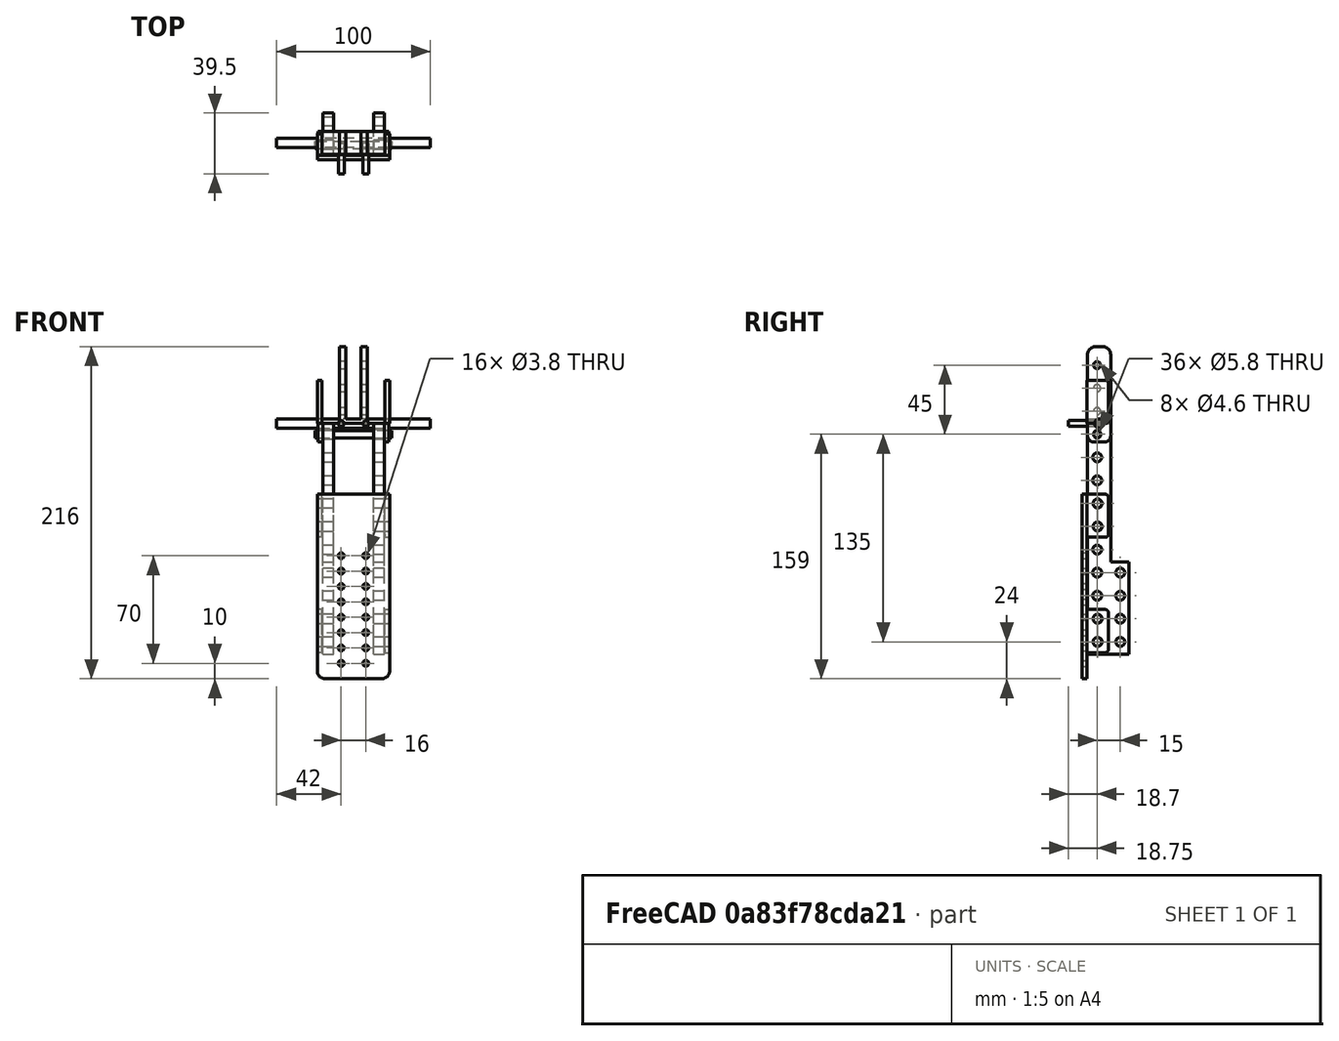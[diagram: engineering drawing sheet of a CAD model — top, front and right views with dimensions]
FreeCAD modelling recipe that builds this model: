
FCSTD DOCUMENT  (FreeCAD 0.20R29410 (Git))
Label: big_cnc_laser_wire_holder
License: All rights reserved
LicenseURL: http://en.wikipedia.org/wiki/All_rights_reserved
objects: Part::Cylinder×83, Part::Box×9, Part::MultiFuse×7, Part::Cut×5, Part::Fuse×4, Part::Fillet×4, Part::Mirroring×4, Part::FeaturePython×4, Part::Compound×2
note: 118 computed .brp shape members not serialized (recipe doc carries the construction recipe); baked Part::Feature solids carry a one-line shape summary decoded from their .brp

FEATURE [Part::Box] cube
  AttacherType = Attacher::AttachEngine3D
  Height = 60
  Length = 7
  Placement = pos=(-3.5,-6,-30) rot=(0,0,1;0rad)
  Width = 12
FEATURE [Part::Box] cube001
  AttacherType = Attacher::AttachEngine3D
  Height = 150
  Length = 7
  Placement = pos=(-3.5,-21,-30) rot=(0,0,1;0rad)
  Width = 15
FEATURE [Part::Fuse] Matrix_Union
  Base = -> cube
  Placement = pos=(16.5,-20,0) rot=(0,0,1;0rad)
  Tool = -> cube001
FEATURE [Part::Cylinder] cylinder
  Angle = 360
  AttacherType = Attacher::AttachEngine3D
  FirstAngle = 0
  Height = 132
  Placement = pos=(-66,0,10) rot=(0,1,0;1.5708rad)
  Radius = 2.9
  SecondAngle = 0
FEATURE [Part::Cylinder] cylinder001 .. cylinder019  x19 (patterned run collapsed; names and placements below)
  Angle = 360
  AttacherType = Attacher::AttachEngine3D
  FirstAngle = 0
  Height = 132
  Radius = 2.9
  SecondAngle = 0
  placements: 19 in arithmetic series — first pos=(-66,0,25) rot=(0,1,0;1.5708rad), step (0,0,15), last pos=(-66,0,295) rot=(0,1,0;1.5708rad)
FEATURE [Part::MultiFuse] Group
  Placement = pos=(0,-19.75,-32) rot=(0,0,1;0rad)
  Shapes = -> [cylinder,cylinder001,cylinder002,cylinder003,cylinder004,cylinder005,cylinder006,cylinder007,cylinder008,cylinder009,cylinder010,cylinder011,cylinder012,cylinder013,cylinder014,cylinder015,cylinder016,cylinder017,cylinder018,cylinder019]
FEATURE [Part::Cylinder] cylinder020 .. cylinder039  x20 (patterned run collapsed; names and placements below)
  Angle = 360
  AttacherType = Attacher::AttachEngine3D
  FirstAngle = 0
  Height = 132
  Radius = 2.9
  SecondAngle = 0
  placements: 20 in arithmetic series — first pos=(-66,0,10) rot=(0,1,0;1.5708rad), step (0,0,15), last pos=(-66,0,295) rot=(0,1,0;1.5708rad)
FEATURE [Part::MultiFuse] Group001
  Placement = pos=(0,-34.75,-32) rot=(0,0,1;0rad)
  Shapes = -> [cylinder020,cylinder021,cylinder022,cylinder023,cylinder024,cylinder025,cylinder026,cylinder027,cylinder028,cylinder029,cylinder030,cylinder031,cylinder032,cylinder033,cylinder034,cylinder035,cylinder036,cylinder037,cylinder038,cylinder039]
FEATURE [Part::Fuse] union
  Base = -> Group
  Tool = -> Group001
FEATURE [Part::Cut] difference
  Base = -> Matrix_Union
  Tool = -> union
FEATURE [Part::Box] cube002
  AttacherType = Attacher::AttachEngine3D
  Height = 60
  Length = 7
  Placement = pos=(-3.5,-6,-30) rot=(0,0,1;0rad)
  Width = 12
FEATURE [Part::Box] cube003
  AttacherType = Attacher::AttachEngine3D
  Height = 150
  Length = 7
  Placement = pos=(-3.5,-21,-30) rot=(0,0,1;0rad)
  Width = 15
FEATURE [Part::Fuse] Matrix_Union001
  Base = -> cube002
  Placement = pos=(-16.5,-20,0) rot=(0,0,1;0rad)
  Tool = -> cube003
FEATURE [Part::Cylinder] cylinder040 .. cylinder059  x20 (patterned run collapsed; names and placements below)
  Angle = 360
  AttacherType = Attacher::AttachEngine3D
  FirstAngle = 0
  Height = 132
  Radius = 2.9
  SecondAngle = 0
  placements: 20 in arithmetic series — first pos=(-66,0,10) rot=(0,1,0;1.5708rad), step (0,0,15), last pos=(-66,0,295) rot=(0,1,0;1.5708rad)
FEATURE [Part::MultiFuse] Group002
  Placement = pos=(0,-19.75,-32) rot=(0,0,1;0rad)
  Shapes = -> [cylinder040,cylinder041,cylinder042,cylinder043,cylinder044,cylinder045,cylinder046,cylinder047,cylinder048,cylinder049,cylinder050,cylinder051,cylinder052,cylinder053,cylinder054,cylinder055,cylinder056,cylinder057,cylinder058,cylinder059]
FEATURE [Part::Cylinder] cylinder060 .. cylinder079  x20 (patterned run collapsed; names and placements below)
  Angle = 360
  AttacherType = Attacher::AttachEngine3D
  FirstAngle = 0
  Height = 132
  Radius = 2.9
  SecondAngle = 0
  placements: 20 in arithmetic series — first pos=(-66,0,10) rot=(0,1,0;1.5708rad), step (0,0,15), last pos=(-66,0,295) rot=(0,1,0;1.5708rad)
FEATURE [Part::MultiFuse] Group003
  Placement = pos=(0,-34.75,-32) rot=(0,0,1;0rad)
  Shapes = -> [cylinder060,cylinder061,cylinder062,cylinder063,cylinder064,cylinder065,cylinder066,cylinder067,cylinder068,cylinder069,cylinder070,cylinder071,cylinder072,cylinder073,cylinder074,cylinder075,cylinder076,cylinder077,cylinder078,cylinder079]
FEATURE [Part::Fuse] union001
  Base = -> Group002
  Tool = -> Group003
FEATURE [Part::Cut] difference001
  Base = -> Matrix_Union001
  Tool = -> union001
FEATURE [Part::Box] Box  label="top panel"
  AttacherType = Attacher::AttachEngine3D
  Height = 3
  Length = 40
  Placement = pos=(-20,-7.5,0) rot=(0,0,1;0rad)
  Width = 15
  expr: .Placement.Base.x = -Length / 2
  expr: .Placement.Base.y = -Width / 2
FEATURE [Part::Compound] Compound
  Links = -> [difference,difference001]
  Placement = pos=(0,33.5,-120) rot=(0,0,1;0rad)
FEATURE [Part::Box] Box001  label="side cube"
  AttacherType = Attacher::AttachEngine3D
  Height = 15
  Length = 3
  Placement = pos=(20,-7.5,-12) rot=(0,0,1;0rad)
  Width = 15
  expr: .Placement.Base.x = <<top panel>>.Length / 2
  expr: .Placement.Base.y = -Width / 2
  expr: .Placement.Base.z = -Height + <<top panel>>.Height
  expr: Width = <<top panel>>.Width
FEATURE [Part::Box] Box002  label="Cube001"
  AttacherType = Attacher::AttachEngine3D
  Height = 50
  Length = 4
  Placement = pos=(5,-7.5,0) rot=(0,0,1;0rad)
  Width = 15
  expr: .Placement.Base.y = -Width / 2
  expr: Width = <<top panel>>.Width
FEATURE [Part::Fillet] Fillet  label="vertical cube fillet"
  Base = -> Box002
  Edges = 2 edges r=5: [Edge10,Edge12]
FEATURE [Part::Mirroring] Part__Mirroring001  label="vertical cube fillet (Mirror #2)"
  Base = (0,0,0)
  Normal = (1,0,0)
  Source = -> Fillet
FEATURE [Part::Cylinder] Cylinder  label="bolt hole"
  Angle = 360
  AttacherType = Attacher::AttachEngine3D
  FirstAngle = 0
  Height = 50
  Placement = pos=(25,-1.3,-7) rot=(0,-1,0;1.5708rad)
  Radius = 2.3
  SecondAngle = 0
  expr: .Placement.Base.x = Height / 2
FEATURE [Part::FeaturePython] Array  label="bolt hole array"  # Draft array (typed FeaturePython)
  AlwaysSyncPlacement = false
  Angle = 360
  ArrayType = 0
  Axis = (0,0,1)
  Base = -> Cylinder
  Center = (0,0,0)
  Count = 4
  ExpandArray = false
  Fuse = false
  IntervalAxis = (0,0,0)
  IntervalX = (100,0,0)
  IntervalY = (0,100,0)
  IntervalZ = (0,0,15)
  NumberCircles = 3
  NumberPolar = 5
  NumberX = 1
  NumberY = 1
  NumberZ = 4
  PlacementList = 4 placements: arithmetic series from (25,-1.3,-7) step (0,0,15) to (25,-1.3,38)
  RadialDistance = 50
  ScaleList = (4) [(1,1,1),(1,1,1),(1,1,1),(1,1,1)]
  Symmetry = 1
  TangentialDistance = 25
FEATURE [Part::Fillet] Fillet001  label="side cube fillet"
  Base = -> Box001
  Edges = 2 edges r=4: [Edge9,Edge11]
FEATURE [Part::Mirroring] Part__Mirroring  label="side cube fillet (Mirror #1)"
  Base = (0,0,0)
  Normal = (1,0,0)
  Source = -> Fillet001
FEATURE [Part::MultiFuse] Fusion
  Shapes = -> [Part__Mirroring,Box,Part__Mirroring001,Fillet,Fillet001]
FEATURE [Part::Cut] Cut  label="wire holder cut"
  Base = -> Fusion
  Tool = -> Array
FEATURE [Part::Box] Box003  label="holder cube"
  AttacherType = Attacher::AttachEngine3D
  Height = 120
  Length = 47
  Placement = pos=(-23.5,-11,-15) rot=(0,0,1;0rad)
  Width = 3
  expr: .Placement.Base.x = -Length / 2
FEATURE [Part::Box] Box004  label="holder side cube"
  AttacherType = Attacher::AttachEngine3D
  Height = 28
  Length = 3
  Placement = pos=(20.5,-8,0) rot=(0,0,1;0rad)
  Width = 14
  expr: .Placement.Base.x = <<holder cube>>.Length / 2 - Length
  expr: .Placement.Base.y = -Width / 2 - 1mm
FEATURE [Part::Fillet] Fillet002  label="holder side fillet"
  Base = -> Box004
  Edges = 2 edges r=2: [Edge11,Edge12]
FEATURE [Part::Mirroring] Part__Mirroring002  label="holder side fillet (Mirror #3)"
  Base = (0,0,0)
  Normal = (1,0,0)
  Source = -> Fillet002
FEATURE [Part::MultiFuse] Fusion001  label="holder side fusion"
  Shapes = -> [Part__Mirroring002,Fillet002]
FEATURE [Part::FeaturePython] Array001  label="holder side fusion array"  # Draft array (typed FeaturePython)
  AlwaysSyncPlacement = false
  Angle = 360
  ArrayType = 0
  Axis = (0,0,1)
  Base = -> Fusion001
  Center = (0,0,0)
  Count = 2
  ExpandArray = false
  Fuse = false
  IntervalAxis = (0,0,0)
  IntervalX = (100,0,0)
  IntervalY = (0,100,0)
  IntervalZ = (0,0,75)
  NumberCircles = 3
  NumberPolar = 5
  NumberX = 1
  NumberY = 1
  NumberZ = 2
  Placement = pos=(0,0,2) rot=(0,0,1;0rad)
  PlacementList = 2 placements: [(0,0,0),(0,0,75)]
  RadialDistance = 50
  ScaleList = (2) [(1,1,1),(1,1,1)]
  Symmetry = 1
  TangentialDistance = 25
FEATURE [Part::Cylinder] Cylinder001  label="side holes"
  Angle = 360
  AttacherType = Attacher::AttachEngine3D
  FirstAngle = 0
  Height = 100
  Placement = pos=(-50,0,0) rot=(0,1,0;1.5708rad)
  Radius = 2.9
  SecondAngle = 0
  expr: .Placement.Base.x = -Height / 2
FEATURE [Part::FeaturePython] Array002  label="side hole array"  # Draft array (typed FeaturePython)
  AlwaysSyncPlacement = false
  Angle = 360
  ArrayType = 0
  Axis = (0,0,1)
  Base = -> Cylinder001
  Center = (0,0,0)
  Count = 10
  ExpandArray = false
  Fuse = false
  IntervalAxis = (0,0,0)
  IntervalX = (100,0,0)
  IntervalY = (0,100,0)
  IntervalZ = (0,0,15)
  NumberCircles = 3
  NumberPolar = 5
  NumberX = 1
  NumberY = 1
  NumberZ = 10
  Placement = pos=(0,-1,9) rot=(0,0,1;0rad)
  PlacementList = 10 placements: arithmetic series from (-50,0,0) step (0,0,15) to (-50,0,135)
  RadialDistance = 50
  ScaleList = (10) [(1,1,1),(1,1,1),(1,1,1),(1,1,1),(1,1,1),(1,1,1),(1,1,1),(1,1,1),(1,1,1),(1,1,1)]
  Symmetry = 1
  TangentialDistance = 25
FEATURE [Part::Cut] Cut001  label="sides with holes"
  Base = -> Array001
  Tool = -> Array002
FEATURE [Part::Fillet] Fillet003  label="holder fillet"
  Base = -> Box003
  Edges = 2 edges r=5: [Edge4,Edge8]
FEATURE [Part::Cylinder] Cylinder002  label="laser attachment hole"
  Angle = 360
  AttacherType = Attacher::AttachEngine3D
  FirstAngle = 0
  Height = 20
  Placement = pos=(8,0,0) rot=(1,0,0;1.5708rad)
  Radius = 1.9
  SecondAngle = 0
FEATURE [Part::Mirroring] Part__Mirroring003  label="laser attachment hole (Mirror #4)"
  Base = (0,0,0)
  Normal = (1,0,0)
  Source = -> Cylinder002
FEATURE [Part::MultiFuse] Fusion002  label="laser hole fusion"
  Shapes = -> [Part__Mirroring003,Cylinder002]
FEATURE [Part::FeaturePython] Array003  label="laser hole array"  # Draft array (typed FeaturePython)
  AlwaysSyncPlacement = false
  Angle = 360
  ArrayType = 0
  Axis = (0,0,1)
  Base = -> Fusion002
  Center = (0,0,0)
  Count = 8
  ExpandArray = false
  Fuse = false
  IntervalAxis = (0,0,0)
  IntervalX = (100,0,0)
  IntervalY = (0,100,0)
  IntervalZ = (0,0,10)
  NumberCircles = 3
  NumberPolar = 5
  NumberX = 1
  NumberY = 1
  NumberZ = 8
  Placement = pos=(0,0,-5) rot=(0,0,1;0rad)
  PlacementList = 8 placements: arithmetic series from (0,0,0) step (0,0,10) to (0,0,70)
  RadialDistance = 50
  ScaleList = (8) [(1,1,1),(1,1,1),(1,1,1),(1,1,1),(1,1,1),(1,1,1),(1,1,1),(1,1,1)]
  Symmetry = 1
  TangentialDistance = 25
FEATURE [Part::Cut] Cut002  label="holder with holes"
  Base = -> Fillet003
  Tool = -> Array003
FEATURE [Part::Compound] Compound001  label="lasertree holder compound"
  Links = -> [Cut001,Cut002]
  Placement = pos=(0,0,-151) rot=(0,0,1;0rad)
